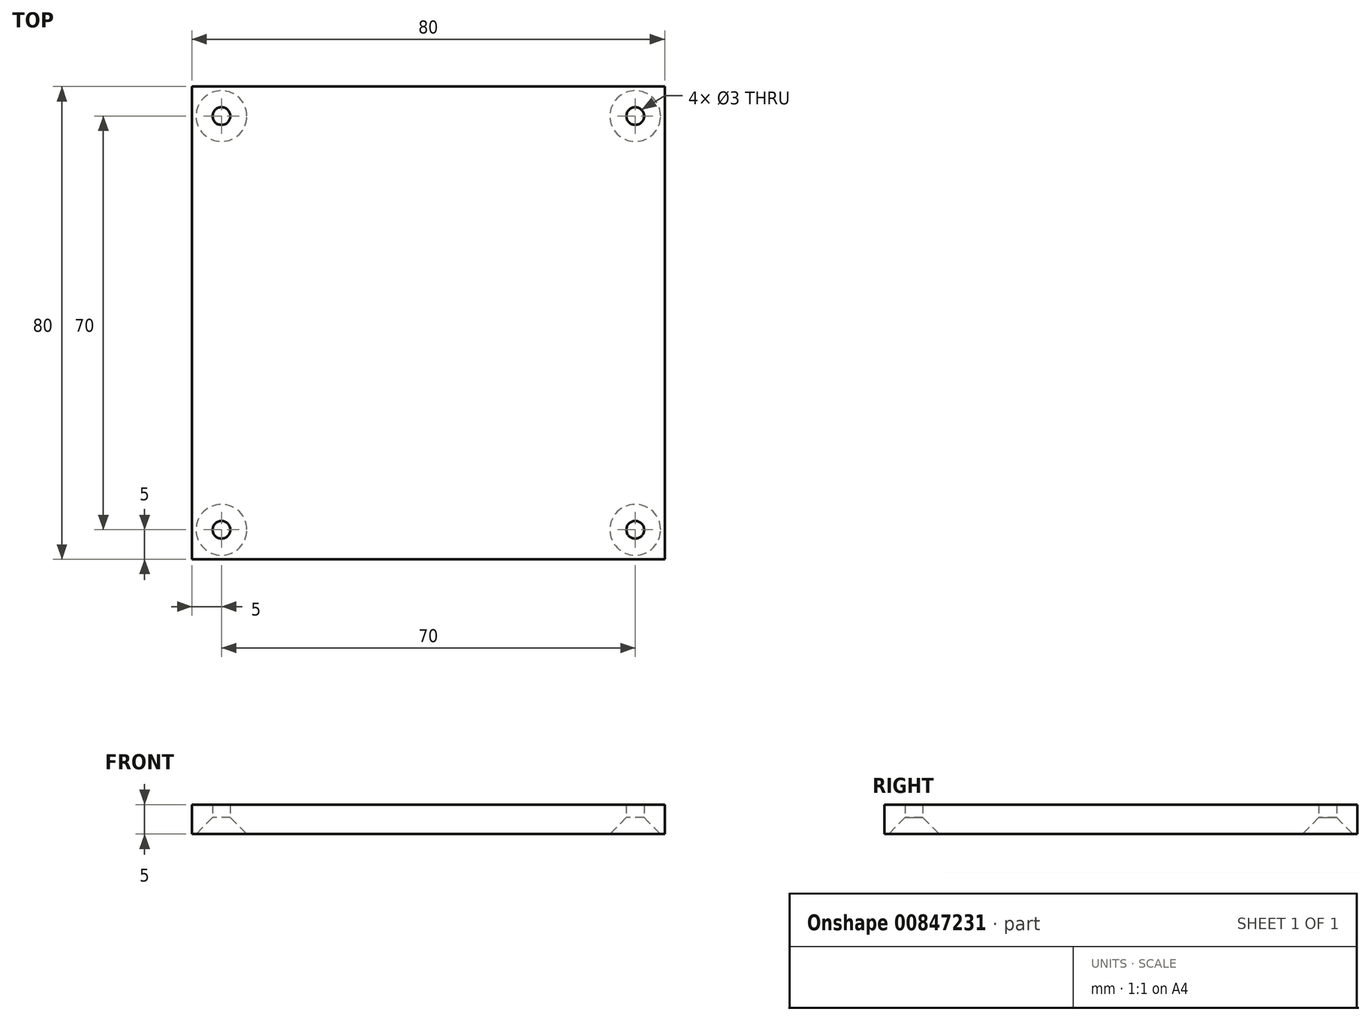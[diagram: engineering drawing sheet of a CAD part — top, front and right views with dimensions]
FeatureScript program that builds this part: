
annotation { "Feature Type Name" : "Feature", "Feature Type Description" : "" }
export const myFeature = defineFeature(function(context is Context, id is Id, definition is map)
    precondition{}
    {
        {
            var Q0;
            Q0=qCreatedBy(makeId("Top.planeOp"),FACE);
            var sketch = newSketch(context, id + "F0", { "sketchPlane" : qUnion([Q0])});
            skLineSegment(sketch, "E0.bottom", {"start": v(40, 40) * mm, "end": v(-40, 40) * mm});
            skLineSegment(sketch, "E0.top", {"start": v(40, -40) * mm, "end": v(-40, -40) * mm});
            skLineSegment(sketch, "E0.left", {"start": v(40, 40) * mm, "end": v(40, -40) * mm});
            skLineSegment(sketch, "E0.right", {"start": v(-40, 40) * mm, "end": v(-40, -40) * mm});
            skPoint(sketch, "E0.middle", {"position": v(0, 0) * mm});
            skCircle(sketch, "E1", {"center": v(-35, 35) * mm, "radius": 1.5 * mm});
            skCircle(sketch, "E2.0.1.0", {"center": v(-35, -35) * mm, "radius": 1.5 * mm});
            skCircle(sketch, "E2.1.0.0", {"center": v(35, 35) * mm, "radius": 1.5 * mm});
            skCircle(sketch, "E2.1.1.0", {"center": v(35, -35) * mm, "radius": 1.5 * mm});
            skLineSegment(sketch, "E2.direction1", {"start": v(-35, 35) * mm, "end": v(35, 35) * mm, "construction": true});
            skLineSegment(sketch, "E2.direction2", {"start": v(-35, 35) * mm, "end": v(-35, -35) * mm, "construction": true});
            skSolve(sketch);
        }
        {
            var Q0;
            Q0=makeQuery(id+"F0.imprint","IMPRINT",FACE,{"disambiguationData":[TD([[makeQuery(id+"F0.imprint","IMPRINT",EDGE,{"derivedFrom":sQuery(id+"F0.wireOp",EDGE,"E0.bottom")}),1.0]])]});
            extrude(context, id + "F1", {"entities" : qUnion([Q0]), "depth" : 5 * mm, "offsetDistance" : 25 * mm});
        }
        {
            var Q0;
            Q0=makeQuery(id+"F1.opExtrude","CAP_EDGE",EDGE,{"disambiguationData":[OSD([sQuery(id+"F0.wireOp",EDGE,"E2.1.0.0")])],"isStart":true});
            var Q1;
            Q1=makeQuery(id+"F1.opExtrude","CAP_EDGE",EDGE,{"disambiguationData":[OSD([sQuery(id+"F0.wireOp",EDGE,"E1")])],"isStart":true});
            var Q2;
            Q2=makeQuery(id+"F1.opExtrude","CAP_EDGE",EDGE,{"disambiguationData":[OSD([sQuery(id+"F0.wireOp",EDGE,"E2.1.1.0")])],"isStart":true});
            var Q3;
            Q3=makeQuery(id+"F1.opExtrude","CAP_EDGE",EDGE,{"disambiguationData":[OSD([sQuery(id+"F0.wireOp",EDGE,"E2.0.1.0")])],"isStart":true});
            chamfer(context, id + "F2", {"entities" : qUnion([Q0, Q1, Q2, Q3]), "chamferType" : ChamferType.OFFSET_ANGLE, "width" : 2.8 * mm, "oppositeDirection" : false, "angle" : 45 * degree, "tangentPropagation" : true});
        }
    });
